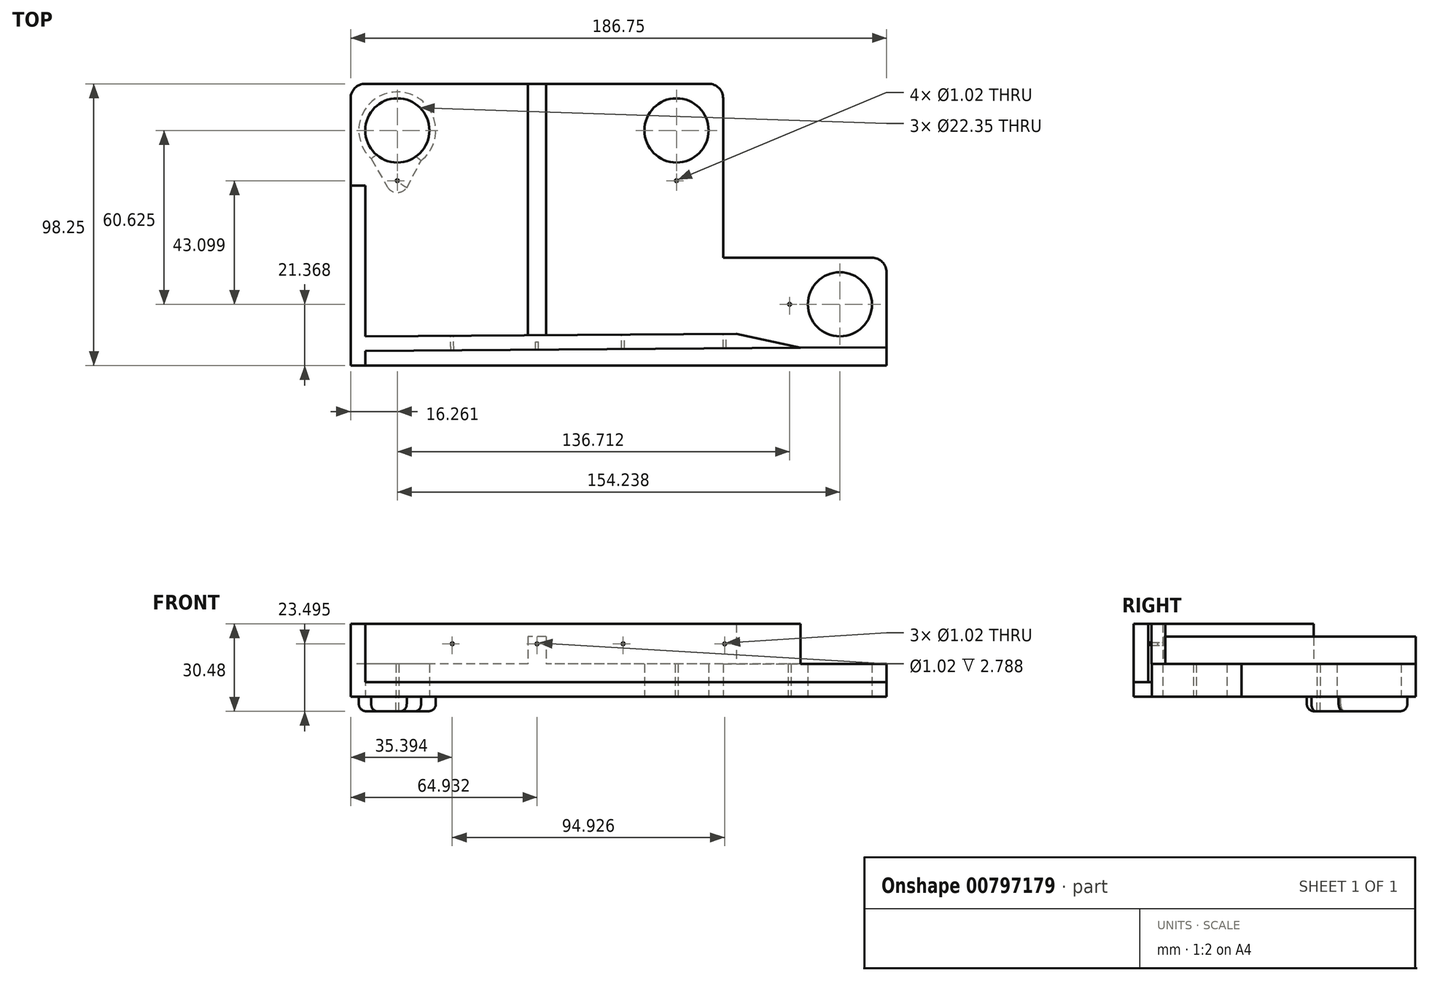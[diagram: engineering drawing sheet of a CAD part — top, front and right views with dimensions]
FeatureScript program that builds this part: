
annotation { "Feature Type Name" : "Feature", "Feature Type Description" : "" }
export const myFeature = defineFeature(function(context is Context, id is Id, definition is map)
    precondition{}
    {
        {
            var Q0;
            Q0=qCreatedBy(makeId("Top.planeOp"),FACE);
            var sketch = newSketch(context, id + "F0", { "sketchPlane" : qUnion([Q0])});
            skCircle(sketch, "E0", {"center": v(-104.26, 68) * mm, "radius": 11.18 * mm});
            skCircle(sketch, "E1", {"center": v(-6.98, 68) * mm, "radius": 11.18 * mm});
            skCircle(sketch, "E2", {"center": v(49.98, 7.38) * mm, "radius": 11.18 * mm});
            skLineSegment(sketch, "E3", {"start": v(9.28, 79.18) * mm, "end": v(9.28, 23.63) * mm});
            skLineSegment(sketch, "E4", {"start": v(9.28, 23.63) * mm, "end": v(61.15, 23.63) * mm});
            skLineSegment(sketch, "E5", {"start": v(66.23, 18.55) * mm, "end": v(66.23, -7.57) * mm});
            skLineSegment(sketch, "E6", {"start": v(66.23, -7.57) * mm, "end": v(-120.52, -8.87) * mm});
            skLineSegment(sketch, "E7", {"start": v(-120.52, -8.87) * mm, "end": v(-120.52, 79.18) * mm});
            skLineSegment(sketch, "E8", {"start": v(4.2, 84.26) * mm, "end": v(-115.44, 84.26) * mm});
            skPoint(sketch, "E9.visualSharp", {"position": v(-120.52, 84.26) * mm});
            skArc(sketch, "E9.filletArc", {"start": v(-115.44, 84.26) * mm, "mid": v(-119.03, 82.77) * mm, "end": v(-120.52, 79.18) * mm});
            skPoint(sketch, "E10.visualSharp", {"position": v(9.28, 84.26) * mm});
            skArc(sketch, "E10.filletArc", {"start": v(9.28, 79.18) * mm, "mid": v(7.8, 82.77) * mm, "end": v(4.2, 84.26) * mm});
            skPoint(sketch, "E11.visualSharp", {"position": v(66.23, 23.63) * mm});
            skArc(sketch, "E11.filletArc", {"start": v(66.23, 18.55) * mm, "mid": v(64.75, 22.15) * mm, "end": v(61.15, 23.63) * mm});
            skCircle(sketch, "E12", {"center": v(-104.26, 50.48) * mm, "radius": 0.5 * mm});
            skCircle(sketch, "E13", {"center": v(-6.98, 50.48) * mm, "radius": 0.5 * mm});
            skCircle(sketch, "E14", {"center": v(32.45, 7.38) * mm, "radius": 0.5 * mm});
            skSolve(sketch);
        }
        {
            var Q0;
            Q0=makeQuery(id+"F0.imprint","IMPRINT",FACE,{"disambiguationData":[TD([[makeQuery(id+"F0.imprint","IMPRINT",EDGE,{"derivedFrom":sQuery(id+"F0.wireOp",EDGE,"E0")}),-1.0]])]});
            extrude(context, id + "F1", {"entities" : qUnion([Q0]), "depth" : 11.43 * mm, "offsetDistance" : 25.4 * mm});
        }
        {
            var Q0;
            Q0=qCreatedBy(makeId("Top.planeOp"),FACE);
            var sketch = newSketch(context, id + "F2", { "sketchPlane" : qUnion([Q0])});
            skLineSegment(sketch, "E15", {"start": v(-120.52, 48.77) * mm, "end": v(-115.44, 48.77) * mm});
            skLineSegment(sketch, "E16", {"start": v(-115.44, 48.77) * mm, "end": v(-115.44, -3.8) * mm});
            skLineSegment(sketch, "E17", {"start": v(-115.44, -3.8) * mm, "end": v(13.91, -2.9) * mm});
            skLineSegment(sketch, "E18", {"start": v(13.91, -2.9) * mm, "end": v(36.26, -7.78) * mm});
            skLineSegment(sketch, "E19", {"start": v(36.26, -7.78) * mm, "end": v(-115.44, -8.87) * mm});
            skLineSegment(sketch, "E20", {"start": v(-115.44, -8.87) * mm, "end": v(-115.4, -13.99) * mm});
            skLineSegment(sketch, "E21", {"start": v(-115.4, -13.99) * mm, "end": v(-120.52, -13.99) * mm});
            skLineSegment(sketch, "E22", {"start": v(-120.52, -13.99) * mm, "end": v(-120.52, 48.77) * mm});
            skSolve(sketch);
        }
        {
            var Q0;
            Q0=makeQuery(id+"F2.imprint","IMPRINT",FACE,{"disambiguationData":[TD([[makeQuery(id+"F2.imprint","IMPRINT",EDGE,{"derivedFrom":sQuery(id+"F2.wireOp",EDGE,"E15")}),-1.0]])]});
            extrude(context, id + "F3", {"entities" : qUnion([Q0]), "operationType" : NewBodyOperationType.ADD, "depth" : 25.4 * mm, "offsetDistance" : 25.4 * mm});
        }
        {
            var Q0;
            Q0=makeQuery(id+"F3.opExtrude","SWEPT_FACE",FACE,{"disambiguationData":[OSD([sQuery(id+"F2.wireOp",EDGE,"E17")])]});
            var sketch = newSketch(context, id + "F4", { "sketchPlane" : qUnion([Q0])});
            skPoint(sketch, "E23", {"position": v(85.16, 11.43) * mm});
            skCircle(sketch, "E24", {"center": v(85.16, 18.42) * mm, "radius": 0.5 * mm});
            skPoint(sketch, "E24.centerSnap0", {"position": v(115.46, 18.42) * mm});
            skCircle(sketch, "E25", {"center": v(-9.77, 18.42) * mm, "radius": 0.5 * mm});
            skCircle(sketch, "E26", {"center": v(25.63, 18.42) * mm, "radius": 0.5 * mm});
            skCircle(sketch, "E27", {"center": v(55.63, 18.42) * mm, "radius": 0.5 * mm});
            skSolve(sketch);
        }
        {
            var Q0;
            Q0=makeQuery(id+"F4.imprint","IMPRINT",FACE,{"disambiguationData":[TD([[makeQuery(id+"F4.imprint","IMPRINT",EDGE,{"derivedFrom":sQuery(id+"F4.wireOp",EDGE,"E25")}),1.0]])]});
            var Q1;
            Q1=makeQuery(id+"F4.imprint","IMPRINT",FACE,{"disambiguationData":[TD([[makeQuery(id+"F4.imprint","IMPRINT",EDGE,{"derivedFrom":sQuery(id+"F4.wireOp",EDGE,"E26")}),1.0]])]});
            var Q2;
            Q2=makeQuery(id+"F4.imprint","IMPRINT",FACE,{"disambiguationData":[TD([[makeQuery(id+"F4.imprint","IMPRINT",EDGE,{"derivedFrom":sQuery(id+"F4.wireOp",EDGE,"E27")}),1.0]])]});
            var Q3;
            Q3=makeQuery(id+"F4.imprint","IMPRINT",FACE,{"disambiguationData":[TD([[makeQuery(id+"F4.imprint","IMPRINT",EDGE,{"derivedFrom":sQuery(id+"F4.wireOp",EDGE,"E24")}),1.0]])]});
            extrude(context, id + "F5", {"entities" : qUnion([Q0, Q1, Q2, Q3]), "operationType" : NewBodyOperationType.REMOVE, "endBound" : BoundingType.THROUGH_ALL, "oppositeDirection" : true, "depth" : 25.4 * mm, "offsetDistance" : 25.4 * mm});
        }
        {
            var Q0;
            Q0=makeQuery(id+"F3.boolean.opBoolean","MERGE",FACE,{"derivedFrom":[makeQuery(id+"F1.opExtrude","SWEPT_FACE",FACE,{"disambiguationData":[OSD([sQuery(id+"F0.wireOp",EDGE,"E7")])]}),makeQuery(id+"F3.opExtrude","SWEPT_FACE",FACE,{"disambiguationData":[OSD([sQuery(id+"F2.wireOp",EDGE,"E22")])]})]});
            var sketch = newSketch(context, id + "F6", { "sketchPlane" : qUnion([Q0])});
            skLineSegment(sketch, "E28.bottom", {"start": v(13.99, 0) * mm, "end": v(7.2, 0) * mm});
            skLineSegment(sketch, "E28.top", {"start": v(13.99, 5.08) * mm, "end": v(7.2, 5.08) * mm});
            skLineSegment(sketch, "E28.left", {"start": v(13.99, 0) * mm, "end": v(13.99, 5.08) * mm});
            skLineSegment(sketch, "E28.right", {"start": v(7.2, 0) * mm, "end": v(7.2, 5.08) * mm});
            skSolve(sketch);
        }
        {
            var Q0;
            Q0=makeQuery(id+"F6.imprint","IMPRINT",FACE,{"disambiguationData":[TD([[makeQuery(id+"F6.imprint","IMPRINT",EDGE,{"derivedFrom":sQuery(id+"F6.wireOp",EDGE,"E28.bottom")}),-1.0]])]});
            extrude(context, id + "F7", {"entities" : qUnion([Q0]), "operationType" : NewBodyOperationType.ADD, "oppositeDirection" : true, "depth" : 186.7 * mm, "offsetDistance" : 25.4 * mm});
        }
        {
            var Q0;
            Q0=makeQuery(id+"F1.opExtrude","SWEPT_FACE",FACE,{"disambiguationData":[OSD([sQuery(id+"F0.wireOp",EDGE,"E8")])]});
            var sketch = newSketch(context, id + "F8", { "sketchPlane" : qUnion([Q0])});
            skLineSegment(sketch, "E29.bottom", {"start": v(52.44, 20.96) * mm, "end": v(58.8, 20.96) * mm});
            skLineSegment(sketch, "E29.top", {"start": v(52.44, 1.9) * mm, "end": v(58.8, 1.9) * mm});
            skLineSegment(sketch, "E29.left", {"start": v(52.44, 20.96) * mm, "end": v(52.44, 1.9) * mm});
            skLineSegment(sketch, "E29.right", {"start": v(58.8, 20.96) * mm, "end": v(58.8, 1.9) * mm});
            skPoint(sketch, "E29.middle", {"position": v(55.62, 11.43) * mm});
            skSolve(sketch);
        }
        {
            var Q0;
            {var subQ0=sQuery(id+"F8.wireOp",EDGE,"E29.bottom");Q0=makeQuery(id+"F8.imprint","IMPRINT",FACE,{"disambiguationData":[TD([[makeQuery(id+"F8.imprint","IMPRINT",EDGE,{"derivedFrom":subQ0}),-1.0]])]});}
            extrude(context, id + "F9", {"entities" : qUnion([Q0]), "operationType" : NewBodyOperationType.ADD, "oppositeDirection" : true, "depth" : 89.92 * mm, "offsetDistance" : 25.4 * mm});
        }
        {
            var Q0;
            Q0=makeQuery(id+"F7.boolean.opBoolean","MERGE",FACE,{"derivedFrom":[makeQuery(id+"F3.boolean.opBoolean","MERGE",FACE,{"derivedFrom":[makeQuery(id+"F1.opExtrude","CAP_FACE",FACE,{"disambiguationData":[OSD([sQuery(id+"F0.wireOp",EDGE,"E0"),sQuery(id+"F0.wireOp",EDGE,"E1"),sQuery(id+"F0.wireOp",EDGE,"E2"),sQuery(id+"F0.wireOp",EDGE,"E3"),sQuery(id+"F0.wireOp",EDGE,"E4"),sQuery(id+"F0.wireOp",EDGE,"E5"),sQuery(id+"F0.wireOp",EDGE,"E6"),sQuery(id+"F0.wireOp",EDGE,"E7"),sQuery(id+"F0.wireOp",EDGE,"E8"),sQuery(id+"F0.wireOp",EDGE,"E9.filletArc"),sQuery(id+"F0.wireOp",EDGE,"E10.filletArc"),sQuery(id+"F0.wireOp",EDGE,"E11.filletArc"),sQuery(id+"F0.wireOp",EDGE,"E12"),sQuery(id+"F0.wireOp",EDGE,"E13"),sQuery(id+"F0.wireOp",EDGE,"E14")])],"isStart":true}),makeQuery(id+"F3.opExtrude","CAP_FACE",FACE,{"disambiguationData":[OSD([sQuery(id+"F2.wireOp",EDGE,"E15"),sQuery(id+"F2.wireOp",EDGE,"E16"),sQuery(id+"F2.wireOp",EDGE,"E17"),sQuery(id+"F2.wireOp",EDGE,"E18"),sQuery(id+"F2.wireOp",EDGE,"E19"),sQuery(id+"F2.wireOp",EDGE,"E20"),sQuery(id+"F2.wireOp",EDGE,"E21"),sQuery(id+"F2.wireOp",EDGE,"E22")])],"isStart":true})]}),makeQuery(id+"F7.opExtrude","SWEPT_FACE",FACE,{"disambiguationData":[OSD([sQuery(id+"F6.wireOp",EDGE,"E28.bottom")])]})]});
            var sketch = newSketch(context, id + "F10", { "sketchPlane" : qUnion([Q0])});
            skCircle(sketch, "E30", {"center": v(-104.26, -68) * mm, "radius": 13.41 * mm});
            skCircle(sketch, "E31", {"center": v(-104.26, -50.48) * mm, "radius": 4.11 * mm});
            skLineSegment(sketch, "E32", {"start": v(-113.35, -58.14) * mm, "end": v(-107.83, -48.44) * mm});
            skLineSegment(sketch, "E33", {"start": v(-100.97, -48) * mm, "end": v(-95.98, -57.45) * mm});
            skSolve(sketch);
        }
        {
            var Q0;
            {var subQ0=sQuery(id+"F10.wireOp",EDGE,"E32");Q0=makeQuery(id+"F10.imprint","IMPRINT",FACE,{"disambiguationData":[TD([[makeQuery(id+"F10.imprint","IMPRINT",EDGE,{"derivedFrom":subQ0}),-1.0]])]});}
            var Q1;
            Q1=makeQuery(id+"F10.imprint","IMPRINT",FACE,{"disambiguationData":[TD([[makeQuery(id+"F10.imprint","IMPRINT",EDGE,{"derivedFrom":makeQuery(id+"F1.opExtrude","CAP_EDGE",EDGE,{"disambiguationData":[OSD([sQuery(id+"F0.wireOp",EDGE,"E12")])],"isStart":true})}),1.0]])]});
            var Q2;
            {var subQ0=sQuery(id+"F10.wireOp",EDGE,"E33");var subQ1=sQuery(id+"F10.wireOp",EDGE,"E30");var subQ2=makeQuery(id+"F10.imprint","INTERSECT",VERTEX,{"derivedFrom":[subQ1,subQ0]});Q2=makeQuery(id+"F10.imprint","IMPRINT",FACE,{"disambiguationData":[TD([[makeQuery(id+"F10.imprint","IMPRINT",EDGE,{"disambiguationData":[TD([[subQ2,-1.0]])],"derivedFrom":subQ1}),-1.0]])]});}
            var Q3;
            Q3=makeQuery(id+"F10.imprint","IMPRINT",FACE,{"disambiguationData":[TD([[makeQuery(id+"F10.imprint","IMPRINT",EDGE,{"derivedFrom":makeQuery(id+"F1.opExtrude","CAP_EDGE",EDGE,{"disambiguationData":[OSD([sQuery(id+"F0.wireOp",EDGE,"E0")])],"isStart":true})}),1.0]])]});
            var Q4;
            Q4=makeQuery(id+"F10.imprint","IMPRINT",FACE,{"disambiguationData":[TD([[makeQuery(id+"F10.imprint","IMPRINT",EDGE,{"derivedFrom":makeQuery(id+"F1.opExtrude","CAP_EDGE",EDGE,{"disambiguationData":[OSD([sQuery(id+"F0.wireOp",EDGE,"E0")])],"isStart":true})}),-1.0]])]});
            extrude(context, id + "F11", {"entities" : qUnion([Q0, Q1, Q2, Q3, Q4]), "depth" : 5.08 * mm, "offsetDistance" : 25.4 * mm});
        }
        {
            var Q0;
            Q0=makeQuery(id+"F11.opExtrude","CAP_EDGE",EDGE,{"disambiguationData":[OSD([sQuery(id+"F10.wireOp",EDGE,"E30")])],"isStart":false});
            var Q1;
            Q1=makeQuery(id+"F11.opExtrude","CAP_EDGE",EDGE,{"disambiguationData":[OSD([sQuery(id+"F10.wireOp",EDGE,"E33")])],"isStart":false});
            var Q2;
            Q2=makeQuery(id+"F11.opExtrude","CAP_EDGE",EDGE,{"disambiguationData":[OSD([sQuery(id+"F10.wireOp",EDGE,"E32")])],"isStart":false});
            var Q3;
            Q3=makeQuery(id+"F11.opExtrude","CAP_EDGE",EDGE,{"disambiguationData":[OSD([sQuery(id+"F10.wireOp",EDGE,"E31")])],"isStart":false});
            fillet(context, id + "F12", {"entities" : qUnion([Q0, Q1, Q2, Q3]), "radius" : 2.54 * mm, "tangentPropagation" : true, "allowEdgeOverflow" : false});
        }
    });
